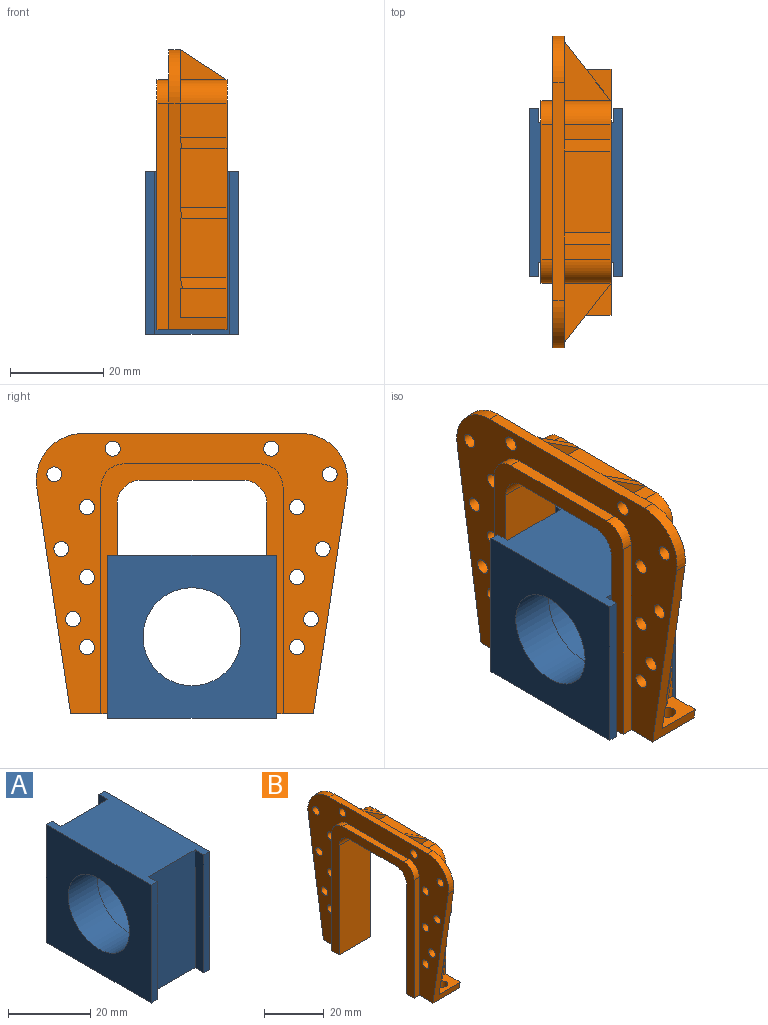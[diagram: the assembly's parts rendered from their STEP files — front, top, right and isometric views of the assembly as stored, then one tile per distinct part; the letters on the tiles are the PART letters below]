
ASSEMBLY  parts=2 mates=1
PART A: 17 faces, bbox 20x36x35 mm
  f0: cylinder r=10.5mm len=21mm, axis (1,0,0), area 659.7mm2, adj f4,f16
  f1: plane 36x20mm, normal (0,0,1), area 624mm2, adj f3,f4,f5,f6,f7,f8,f9,f10
  f2: plane 36x20mm, normal (0,0,-1), area 624mm2, adj f3,f4,f5,f6,f7,f8,f9,f10
  f3: plane 36x35mm, normal (1,0,0), area 807.6mm2, adj f1,f2,f12,f14,f15
  f4: plane 36x35mm, normal (-1,0,0), area 913.6mm2, adj f0,f1,f2,f11,f13
  f5: plane 35x3mm, normal (1,0,0), area 105mm2, adj f1,f2,f6,f13
  f6: plane 35x16mm, normal (0,1,0), area 560mm2, adj f1,f2,f5,f7
  f7: plane 35x3mm, normal (-1,0,0), area 105mm2, adj f1,f2,f6,f14
  f8: plane 35x3mm, normal (1,0,0), area 105mm2, adj f1,f2,f10,f11
  f9: plane 35x3mm, normal (-1,0,0), area 105mm2, adj f1,f2,f10,f12
  f10: plane 35x16mm, normal (0,-1,0), area 560mm2, adj f1,f2,f8,f9
  f11: plane 35x2mm, normal (0,-1,0), area 70mm2, adj f1,f2,f4,f8
  f12: plane 35x2mm, normal (0,-1,0), area 70mm2, adj f1,f2,f3,f9
  f13: plane 35x2mm, normal (0,1,0), area 70mm2, adj f1,f2,f4,f5
  f14: plane 35x2mm, normal (0,1,0), area 70mm2, adj f1,f2,f3,f7
  f15: cylinder r=12mm len=24mm, axis (1,0,0), area 754mm2, adj f3,f16
  f16: plane 24x24mm, normal (1,0,0), area 106mm2, adj f0,f15
PART B: 84 faces, bbox 15x66.7x60 mm
  f0: plane 66.74x60mm, normal (-1,0,0), area 1409.9mm2, adj f1,f2,f43,f44,f45,f46,f47,f51
  f1: plane 15x10mm, normal (0,0,-1), area 123.6mm2, adj f0,f3,f40,f47,f50,f55,f82
  f2: plane 15x10mm, normal (0,0,-1), area 123.6mm2, adj f0,f3,f42,f43,f50,f54,f83
  f3: plane 53.5x52.75mm, normal (1,0,0), area 519.9mm2, adj f1,f2,f4,f5,f6,f7,f8,f9
  f4: plane 12.67x10mm, normal (0.78,-0.62,0), area 39.8mm2, adj f3,f20,f21,f47
  f5: plane 10x8.18mm, normal (0.63,-0.77,0), area 31.6mm2, adj f3,f18,f19,f47
  f6: plane 10.43x10mm, normal (0.72,-0.69,0), area 35.5mm2, adj f3,f12,f13,f47
  f7: plane 10x6.87mm, normal (0,0,1), area 58.6mm2, adj f3,f10,f11,f43,f83
  f8: plane 10x6.87mm, normal (0,0,1), area 58.6mm2, adj f3,f9,f31,f47,f82
  f9: plane 10x6.25mm, normal (0,-1,0), area 62.5mm2, adj f3,f8,f19,f31
  f10: plane 10x6.25mm, normal (0,1,0), area 62.5mm2, adj f3,f7,f11,f16
  f11: plane 7.81x6.25mm, normal (1,0,0), area 45.9mm2, adj f7,f10,f16,f43
  f12: plane 10.43x10mm, normal (0,0,1), area 52.1mm2, adj f6,f32,f35
  f13: plane 10.05x10mm, normal (0,0,-1), area 52.1mm2, adj f6,f30,f33,f47
  f14: plane 10x8.18mm, normal (0,0,1), area 40.9mm2, adj f24,f25,f67
  f15: plane 10.43x10mm, normal (0,0,1), area 52.1mm2, adj f26,f27,f66
  f16: plane 10x7.81mm, normal (0,0,-1), area 40.8mm2, adj f10,f11,f43,f67
  f17: plane 12.67x10mm, normal (0,0,1), area 63.4mm2, adj f28,f29,f65
  f18: plane 10x8.18mm, normal (0,0,1), area 40.9mm2, adj f5,f30,f33
  f19: plane 10x7.81mm, normal (0,0,-1), area 40.8mm2, adj f5,f9,f31,f47
  f20: plane 12.67x10mm, normal (0,0,1), area 63.4mm2, adj f4,f34,f39
  f21: plane 12.3x10mm, normal (0,0,-1), area 63.3mm2, adj f4,f32,f35,f47
  f22: plane 10x6.5mm, normal (0,1,0), area 32.5mm2, adj f29,f57,f64
  f23: plane 10x6.5mm, normal (0,1,0), area 32.5mm2, adj f36,f37,f63
  f24: plane 12.5x10mm, normal (0,1,0), area 125mm2, adj f3,f14,f25,f62
  f25: plane 12.5x10.05mm, normal (1,0,0), area 97.9mm2, adj f14,f24,f43,f62,f74,f75
  f26: plane 12.5x10mm, normal (0,1,0), area 125mm2, adj f3,f15,f27,f61
  f27: plane 12.5x12.3mm, normal (1,0,0), area 125.9mm2, adj f15,f26,f43,f61,f69,f76
  f28: plane 10x7.25mm, normal (0,1,0), area 72.5mm2, adj f3,f17,f29,f56
  f29: plane 22.12x18.75mm, normal (1,0,0), area 268.6mm2, adj f17,f22,f28,f43,f44,f45,f56,f57
  f30: plane 12.5x10mm, normal (0,-1,0), area 125mm2, adj f3,f13,f18,f33
  f31: plane 7.81x6.25mm, normal (1,0,0), area 45.9mm2, adj f8,f9,f19,f47
  f32: plane 12.5x10mm, normal (0,-1,0), area 125mm2, adj f3,f12,f21,f35
  f33: plane 12.5x10.05mm, normal (1,0,0), area 97.9mm2, adj f13,f18,f30,f47,f72,f80
  f34: plane 10x7.25mm, normal (0,-1,0), area 72.5mm2, adj f3,f20,f39,f58
  f35: plane 12.5x12.3mm, normal (1,0,0), area 125.9mm2, adj f12,f21,f32,f47,f71,f79
  f36: plane 17.5x10mm, normal (0,0,1), area 175mm2, adj f3,f23,f37,f60
  f37: plane 17.5x6.5mm, normal (1,0,0), area 113.7mm2, adj f23,f36,f45,f60
  f38: plane 10x3.25mm, normal (0,0,1), area 32.5mm2, adj f3,f39,f58,f59
  f39: plane 22.12x18.75mm, normal (1,0,0), area 268.6mm2, adj f20,f34,f38,f45,f46,f47,f58,f59
  f40: plane 45x15mm, normal (0,1,0), area 675mm2, adj f1,f3,f48,f50
  f41: plane 22x15mm, normal (0,0,-1), area 330mm2, adj f3,f48,f49,f50
  f42: plane 45x15mm, normal (0,-1,0), area 675mm2, adj f2,f3,f49,f50
  f43: plane 48.52x12.5mm, normal (0,0.99,-0.15), area 149.3mm2, adj f0,f2,f3,f7,f11,f16,f25,f27
  f44: cylinder r=10mm len=11.48mm, axis (-1,0,0), area 43mm2, adj f0,f29,f43,f45
  f45: plane 46.74x2.5mm, normal (0,0,1), area 116.8mm2, adj f0,f29,f37,f39,f44,f46,f63,f64
  f46: cylinder r=10mm len=11.48mm, axis (-1,0,0), area 43mm2, adj f0,f39,f45,f47
  f47: plane 48.52x12.5mm, normal (0,-0.99,-0.15), area 149.3mm2, adj f0,f1,f3,f4,f5,f6,f8,f13
  f48: cylinder r=5mm len=15mm, axis (-1,0,0), area 117.8mm2, adj f3,f40,f41,f50
  f49: cylinder r=5mm len=15mm, axis (1,0,0), area 117.8mm2, adj f3,f41,f42,f50
  f50: plane 53.5x39mm, normal (-1,0,0), area 486.5mm2, adj f1,f2,f40,f41,f42,f48,f49,f51
  f51: cylinder r=5mm len=5mm, axis (-1,0,0), area 19.6mm2, adj f0,f50,f52,f55
  f52: plane 29x2.5mm, normal (0,0,1), area 72.5mm2, adj f0,f50,f51,f53
  f53: cylinder r=5mm len=5mm, axis (-1,0,0), area 19.6mm2, adj f0,f50,f52,f54
  f54: plane 48.5x2.5mm, normal (0,1,0), area 121.3mm2, adj f0,f2,f50,f53
  f55: plane 48.5x2.5mm, normal (0,-1,0), area 121.3mm2, adj f0,f1,f50,f51
  f56: cylinder r=5mm len=10mm, axis (-1,0,0), area 78.5mm2, adj f3,f28,f29,f57
  f57: plane 10x3.25mm, normal (0,0,1), area 32.5mm2, adj f3,f22,f29,f56
  f58: cylinder r=5mm len=10mm, axis (-1,0,0), area 78.5mm2, adj f3,f34,f38,f39
  f59: plane 10x6.5mm, normal (0,-1,0), area 32.5mm2, adj f38,f39,f63
  f60: plane 10x6.5mm, normal (0,-1,0), area 32.5mm2, adj f36,f37,f64
  f61: plane 12.3x10mm, normal (0,0,-1), area 63.3mm2, adj f26,f27,f43,f65
  f62: plane 10.05x10mm, normal (0,0,-1), area 52.1mm2, adj f24,f25,f43,f66
  f63: plane 10x6.5mm, normal (0.54,0,0.84), area 29.8mm2, adj f3,f23,f45,f59
  f64: plane 10x6.5mm, normal (0.54,0,0.84), area 29.8mm2, adj f3,f22,f45,f60
  f65: plane 12.67x10mm, normal (0.78,0.62,0), area 39.8mm2, adj f3,f17,f43,f61
  f66: plane 10.43x10mm, normal (0.72,0.69,0), area 35.5mm2, adj f3,f15,f43,f62
  f67: plane 10x8.18mm, normal (0.63,0.77,0), area 31.6mm2, adj f3,f14,f16,f43
  f68: cylinder r=1.6mm len=3.2mm, axis (1,0,0), area 25.1mm2, adj f0,f39
  f69: cylinder r=1.6mm len=3.2mm, axis (1,0,0), area 25.1mm2, adj f0,f27
  f70: cylinder r=1.6mm len=3.2mm, axis (1,0,0), area 25.1mm2, adj f0,f29
  f71: cylinder r=1.6mm len=3.2mm, axis (1,0,0), area 25.1mm2, adj f0,f35
  f72: cylinder r=1.6mm len=3.2mm, axis (1,0,0), area 25.1mm2, adj f0,f33
  f73: cylinder r=1.6mm len=3.2mm, axis (1,0,0), area 25.1mm2, adj f0,f39
  f74: cylinder r=1.6mm len=3.2mm, axis (1,0,0), area 25.1mm2, adj f0,f25
  f75: cylinder r=1.6mm len=3.2mm, axis (1,0,0), area 25.1mm2, adj f0,f25
  f76: cylinder r=1.6mm len=3.2mm, axis (1,0,0), area 25.1mm2, adj f0,f27
  f77: cylinder r=1.6mm len=3.2mm, axis (1,0,0), area 25.1mm2, adj f0,f29
  f78: cylinder r=1.6mm len=3.2mm, axis (1,0,0), area 25.1mm2, adj f0,f39
  f79: cylinder r=1.6mm len=3.2mm, axis (1,0,0), area 25.1mm2, adj f0,f35
  f80: cylinder r=1.6mm len=3.2mm, axis (1,0,0), area 25.1mm2, adj f0,f33
  f81: cylinder r=1.6mm len=3.2mm, axis (1,0,0), area 25.1mm2, adj f0,f29
  f82: cylinder r=1.8mm len=3.6mm, axis (0,0,1), area 28.3mm2, adj f1,f8
  f83: cylinder r=1.8mm len=3.6mm, axis (0,0,1), area 28.3mm2, adj f2,f7
PLACE A t=(-11.02,-40.36,51.97)mm
PLACE B t=(-6.02,-42.41,65.3)mm fixed
MATE slider A.f1 <-> B.f41  axis (0,0,1) through (-1.02,-29.72,46.89)mm
